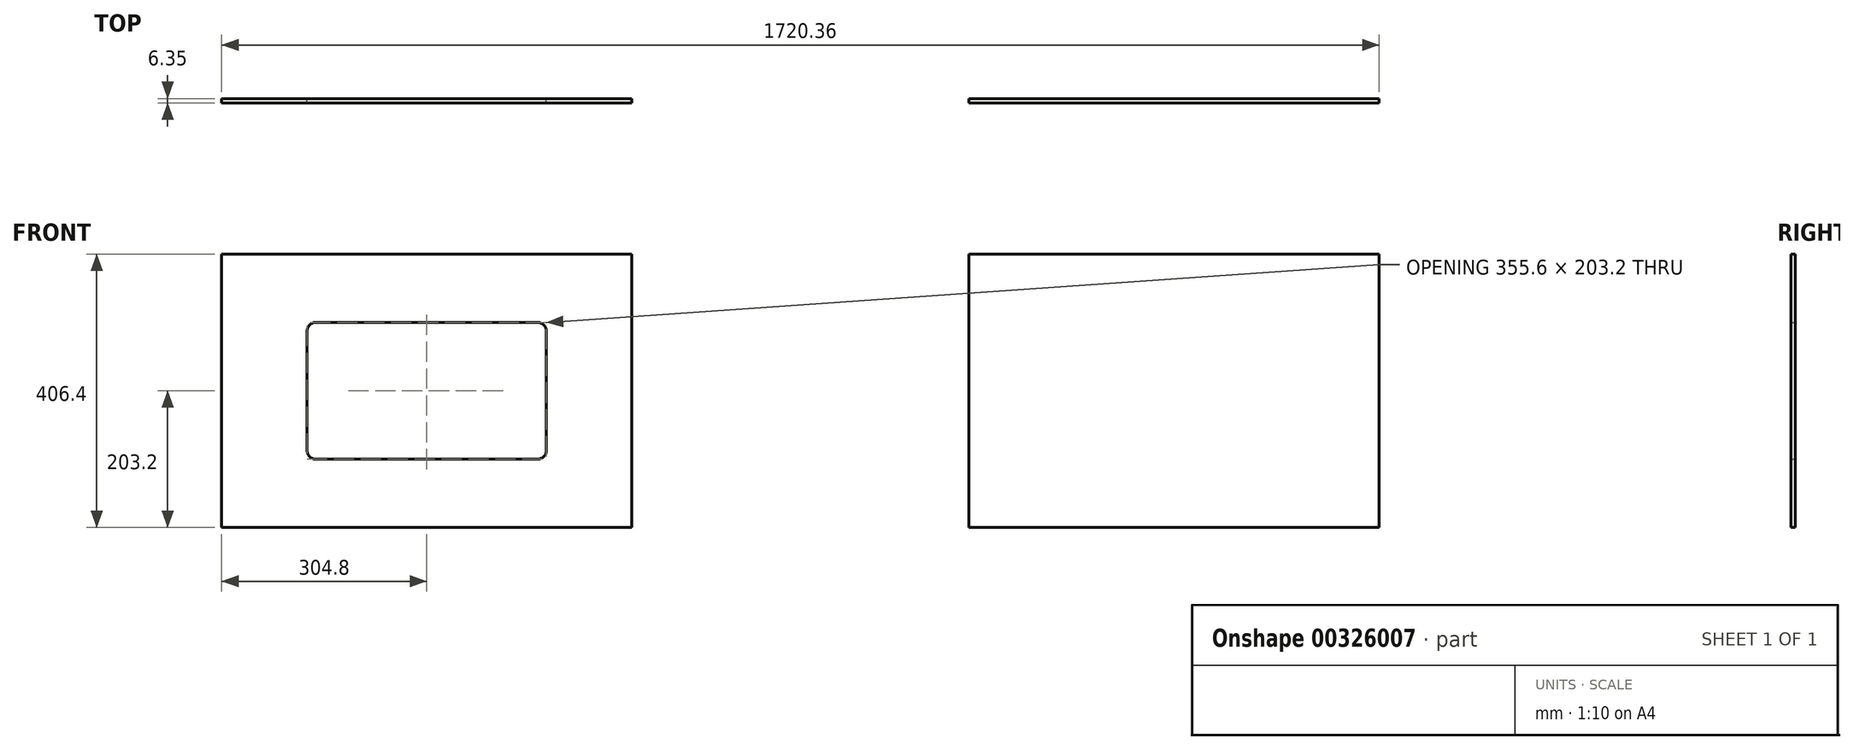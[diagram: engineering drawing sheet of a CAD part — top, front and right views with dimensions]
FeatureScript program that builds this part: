
annotation { "Feature Type Name" : "Feature", "Feature Type Description" : "" }
export const myFeature = defineFeature(function(context is Context, id is Id, definition is map)
    precondition{}
    {
        {
            var Q0;
            Q0=qCreatedBy(makeId("Front.planeOp"),FACE);
            var sketch = newSketch(context, id + "F0", { "sketchPlane" : qUnion([Q0])});
            skLineSegment(sketch, "E0.bottom", {"start": v(304.8, -203.2) * mm, "end": v(-304.8, -203.2) * mm});
            skLineSegment(sketch, "E0.top", {"start": v(304.8, 203.2) * mm, "end": v(-304.8, 203.2) * mm});
            skLineSegment(sketch, "E0.left", {"start": v(304.8, -203.2) * mm, "end": v(304.8, 203.2) * mm});
            skLineSegment(sketch, "E0.right", {"start": v(-304.8, -203.2) * mm, "end": v(-304.8, 203.2) * mm});
            skPoint(sketch, "E0.middle", {"position": v(0, 0) * mm});
            skLineSegment(sketch, "E1.bottom", {"start": v(177.8, -101.6) * mm, "end": v(-177.8, -101.6) * mm});
            skLineSegment(sketch, "E1.top", {"start": v(177.8, 101.6) * mm, "end": v(-177.8, 101.6) * mm});
            skLineSegment(sketch, "E1.left", {"start": v(177.8, -101.6) * mm, "end": v(177.8, 101.6) * mm});
            skLineSegment(sketch, "E1.right", {"start": v(-177.8, -101.6) * mm, "end": v(-177.8, 101.6) * mm});
            skSolve(sketch);
        }
        {
            var Q0;
            Q0 = qSketchRegion(id + "F0", true);
            extrude(context, id + "F1", {"entities" : qUnion([Q0]), "depth" : 6.35 * mm});
        }
        {
            var Q0;
            Q0=makeQuery(id+"F1.opExtrude","SWEPT_EDGE",EDGE,{"disambiguationData":[OSD([sQuery(id+"F0.wireOp",EDGE,"E1.top"),sQuery(id+"F0.wireOp",EDGE,"E1.right")])]});
            var Q1;
            Q1=makeQuery(id+"F1.opExtrude","SWEPT_EDGE",EDGE,{"disambiguationData":[OSD([sQuery(id+"F0.wireOp",EDGE,"E1.top"),sQuery(id+"F0.wireOp",EDGE,"E1.left")])]});
            var Q2;
            Q2=makeQuery(id+"F1.opExtrude","SWEPT_EDGE",EDGE,{"disambiguationData":[OSD([sQuery(id+"F0.wireOp",EDGE,"E1.bottom"),sQuery(id+"F0.wireOp",EDGE,"E1.left")])]});
            var Q3;
            Q3=makeQuery(id+"F1.opExtrude","SWEPT_EDGE",EDGE,{"disambiguationData":[OSD([sQuery(id+"F0.wireOp",EDGE,"E1.bottom"),sQuery(id+"F0.wireOp",EDGE,"E1.right")])]});
            fillet(context, id + "F2", {"entities" : qUnion([Q0, Q1, Q2, Q3]), "radius" : 12.7 * mm, "tangentPropagation" : true, "allowEdgeOverflow" : false});
        }
        {
            var Q0;
            Q0=qCreatedBy(makeId("Front.planeOp"),FACE);
            var sketch = newSketch(context, id + "F3", { "sketchPlane" : qUnion([Q0])});
            skLineSegment(sketch, "E2.bottom", {"start": v(805.96, 203.2) * mm, "end": v(1415.56, 203.2) * mm});
            skLineSegment(sketch, "E2.top", {"start": v(805.96, -203.2) * mm, "end": v(1415.56, -203.2) * mm});
            skLineSegment(sketch, "E2.left", {"start": v(805.96, 203.2) * mm, "end": v(805.96, -203.2) * mm});
            skLineSegment(sketch, "E2.right", {"start": v(1415.56, 203.2) * mm, "end": v(1415.56, -203.2) * mm});
            skPoint(sketch, "E2.middle", {"position": v(1110.76, 0) * mm});
            skSolve(sketch);
        }
        {
            var Q0;
            Q0=makeQuery(id+"F3.imprint","IMPRINT",FACE,{"disambiguationData":[TD([[makeQuery(id+"F3.imprint","IMPRINT",EDGE,{"derivedFrom":sQuery(id+"F3.wireOp",EDGE,"E2.bottom")}),-1.0]])]});
            extrude(context, id + "F4", {"entities" : qUnion([Q0]), "depth" : 6.35 * mm});
        }
    });
